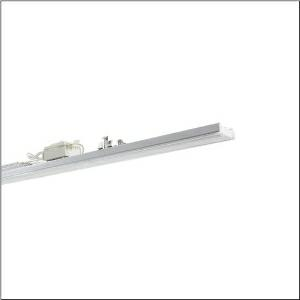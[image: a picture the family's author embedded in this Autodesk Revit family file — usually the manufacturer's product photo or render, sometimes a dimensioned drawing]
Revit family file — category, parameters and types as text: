
# Revit family: licross_r__11_recessed_mo_51tl12de45xg_48c6
name_source: partatom
category: Lighting Fixtures
units: mm (PartAtom-declared; Revit-internal decimal feet)

## family parameters
Cut with Voids When Loaded = No
Host = Face
Light Source = No
Part Type = Normal
Room Calculation Point = No
Round Connector Dimension = Use Diameter
Shared = No

## types (1)
- --- (1 x LED, 5120 lm, 29.6 W, 4000K)
    Apparent Load = 30 VA
    CIE Flux Codes = 67 92 99 100 100
    Color Rendering = 80
    Color Temperature = 4000K
    Default Elevation = 1800 mm
    Description = Licross® 11 Recessed MO, luminaire insert, of sheet steel, coil coated, white, length: 750mm, width: 66mm, height: 67mm, LED rated luminous flux: 5.120lm, light colour: 840, control gear: DALI 2, with plug, 5-pole, with phase selection, mains connection: 220..240V, AC, 50/60Hz, rated input power: 30W, halogen-free wiring, primary optical cover: cover, of PMMA, light emission: direct distribution, primary light characteristic: symmetric, protection rating (complete): IP40, insulation class (complete): insulation class I (protective earthing), certification: CE, ENEC, VDE, UKCA, protection symbol: D if used in an environment without relevant dust loads with corresponding accessories, impact resistance: IK06, permissible ambient temperature for indoor applications: -25..+35°C, corresponds to IFS (International Featured Standards) requirements for safety and quality in the food industry, reducing of maximum allowable ambient temperature of 5°C with ceiling mounting, LABS conformity tested according to VDMA 24364:2018-05, packaging unit: 1 piece
    Height = 58 mm
    Lamp = 1 x LED
    Lamp Light Flux = 5120 lm
    Lamp Power = 29.6 W
    Lamp count = 1
    Length = 750 mm
    Luminous efficacy = 173 lm/W
    Manufacturer = Siteco
    ModVariant = No
    Model = 51TL12DE45XG
    Mounting Place = Ceiling
    Mounting Type = Pendant
    Number of Poles = 1
    OnlyDefault = Yes
    Power Factor = 1
    Product Name = Licross® 11 Recessed MO
    Product group = luminaire insert
    ProductGroupID = 902
    Protection Class = Protection class I
    Protection Degree = IP 40
    RLX_Detail_Level = 1
    RLX_Emergency_Light_Flux = 0 lm
    RLX_Emergency_Type = 0
    RLX_Emergency_Type_DB = No
    RlxData = <blob elided: 28917 chars, md5=1e420516>
    Socket = socket
    Standby Power = 0 W
    System Light Flux = 5120 lm
    System Power = 30 W
    Type Comments = factory setting: luminous flux: 100 % | dim-lin: 254 | 378 mA
    Type Image = l_1296930.jpg
    URL = http://relux.com
    VarID = @adj_100150
    Voltage = 0 V
    Weight = 0.00 kg
    Width = 66 mm

## geometry (parser evidence)
native form markers: Blend x4, Sweep x11
no freeform markers — native parametric forms only
